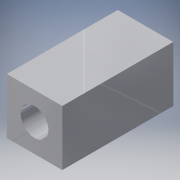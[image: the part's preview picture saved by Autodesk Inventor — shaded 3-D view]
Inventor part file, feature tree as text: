
AUTODESK INVENTOR PART (.ipt)
format: ipt  version: 2016 (Build 200138000, 138)  size: 92,672 bytes
history: native  units: in
note: dims shown in document units (in); Inventor stores cm internally (conversion verified against a paired STEP export)
features: extrude x1, sketch x1
ambient origin geometry x8: Origin, YZ Plane, XZ Plane, XY Plane, X Axis, Y Axis, Z Axis, Center Point
bodies: Solid1 (feature_tree)
feature tree (2):
  extrude  "Extrusion1"  Depth=0.5in
  sketch  "Sketch1"  dims[d0=0.25in d1=0.5in d2=0.5in d3=0.25in d4=0.25in d5=1.0in d6=0.0in]
